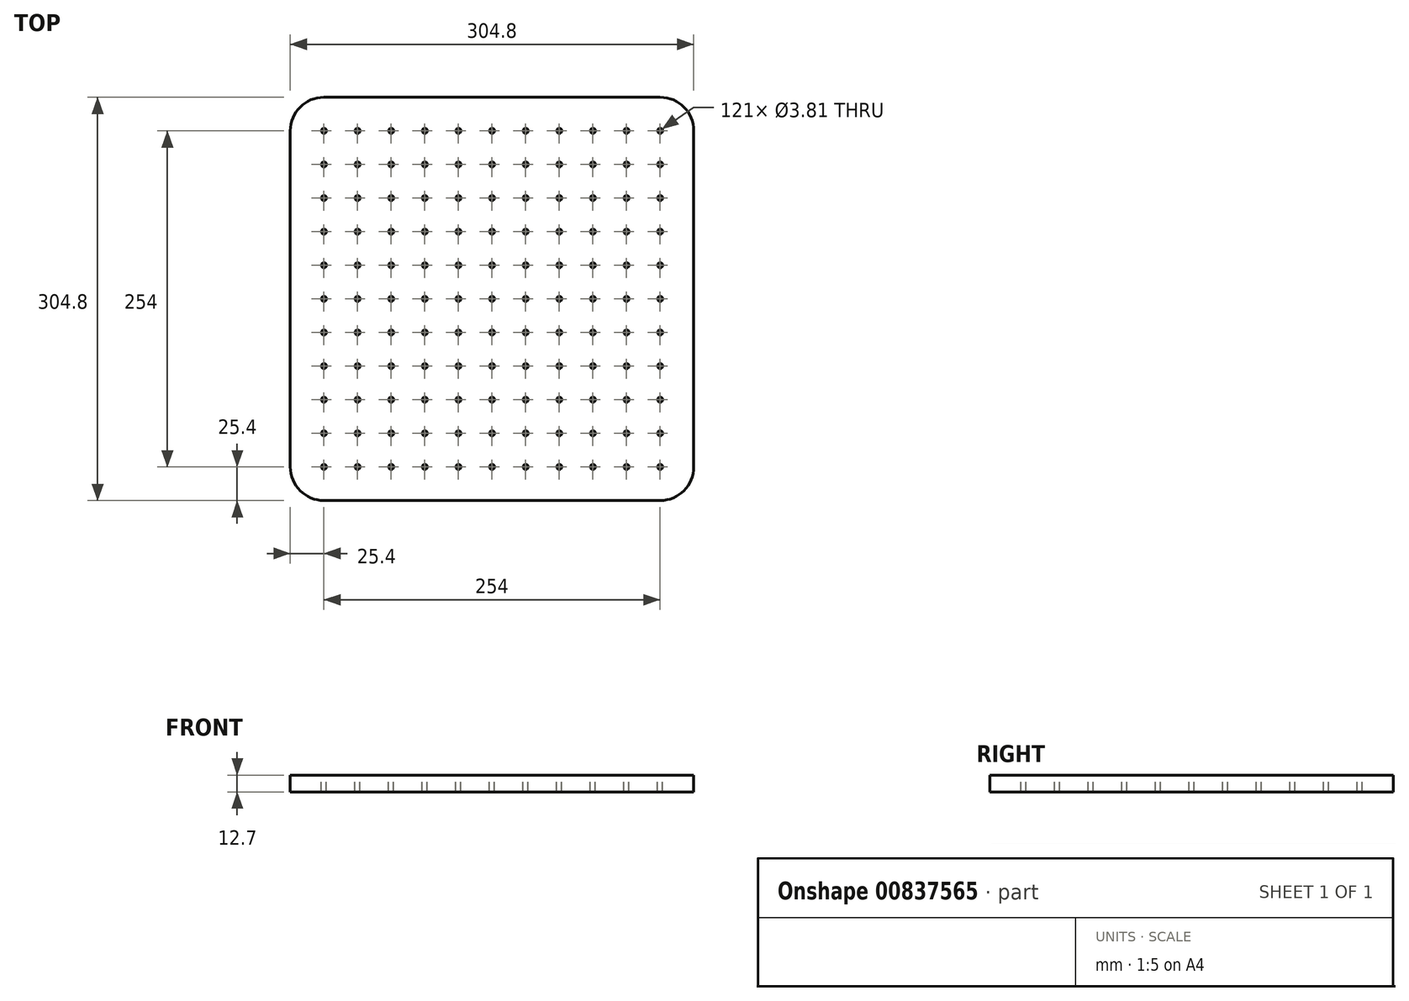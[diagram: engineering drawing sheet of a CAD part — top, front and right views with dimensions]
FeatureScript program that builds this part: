
annotation { "Feature Type Name" : "Feature", "Feature Type Description" : "" }
export const myFeature = defineFeature(function(context is Context, id is Id, definition is map)
    precondition{}
    {
        {
            var Q0;
            Q0=qCreatedBy(makeId("Top.planeOp"),FACE);
            var sketch = newSketch(context, id + "F0", { "sketchPlane" : qUnion([Q0])});
            skLineSegment(sketch, "E0.bottom", {"start": v(127, 152.4) * mm, "end": v(-127, 152.4) * mm});
            skLineSegment(sketch, "E0.top", {"start": v(127, -152.4) * mm, "end": v(-127, -152.4) * mm});
            skLineSegment(sketch, "E0.left", {"start": v(152.4, 127) * mm, "end": v(152.4, -127) * mm});
            skLineSegment(sketch, "E0.right", {"start": v(-152.4, 127) * mm, "end": v(-152.4, -127) * mm});
            skPoint(sketch, "E0.middle", {"position": v(0, 0) * mm});
            skCircle(sketch, "E1", {"center": v(-127, 127) * mm, "radius": 1.9 * mm});
            skLineSegment(sketch, "E2", {"start": v(-127, 127) * mm, "end": v(-127, 152.4) * mm, "construction": true});
            skLineSegment(sketch, "E3", {"start": v(-152.4, 127) * mm, "end": v(-127, 127) * mm, "construction": true});
            skCircle(sketch, "E4.0.1.0", {"center": v(-127, 101.6) * mm, "radius": 1.9 * mm});
            skCircle(sketch, "E4.1.0.0", {"center": v(-101.6, 127) * mm, "radius": 1.9 * mm});
            skCircle(sketch, "E4.1.1.0", {"center": v(-101.6, 101.6) * mm, "radius": 1.9 * mm});
            skCircle(sketch, "E4.2.0.0", {"center": v(-76.2, 127) * mm, "radius": 1.9 * mm});
            skCircle(sketch, "E4.2.1.0", {"center": v(-76.2, 101.6) * mm, "radius": 1.9 * mm});
            skLineSegment(sketch, "E4.direction1", {"start": v(-127, 127) * mm, "end": v(-101.6, 127) * mm, "construction": true});
            skLineSegment(sketch, "E4.direction2", {"start": v(-127, 127) * mm, "end": v(-127, 101.6) * mm, "construction": true});
            skCircle(sketch, "E5.0.0.2", {"center": v(-127, 76.2) * mm, "radius": 1.9 * mm});
            skCircle(sketch, "E5.0.0.3", {"center": v(-127, 50.8) * mm, "radius": 1.9 * mm});
            skCircle(sketch, "E5.0.0.4", {"center": v(-127, 25.4) * mm, "radius": 1.9 * mm});
            skCircle(sketch, "E5.0.0.5", {"center": v(-127, 0) * mm, "radius": 1.9 * mm});
            skCircle(sketch, "E5.0.0.6", {"center": v(-127, -25.4) * mm, "radius": 1.9 * mm});
            skCircle(sketch, "E5.0.0.7", {"center": v(-127, -50.8) * mm, "radius": 1.9 * mm});
            skCircle(sketch, "E5.0.0.8", {"center": v(-127, -76.2) * mm, "radius": 1.9 * mm});
            skCircle(sketch, "E5.0.0.9", {"center": v(-127, -101.6) * mm, "radius": 1.9 * mm});
            skCircle(sketch, "E5.0.1.2", {"center": v(-101.6, 76.2) * mm, "radius": 1.9 * mm});
            skCircle(sketch, "E5.0.1.3", {"center": v(-101.6, 50.8) * mm, "radius": 1.9 * mm});
            skCircle(sketch, "E5.0.1.4", {"center": v(-101.6, 25.4) * mm, "radius": 1.9 * mm});
            skCircle(sketch, "E5.0.1.5", {"center": v(-101.6, 0) * mm, "radius": 1.9 * mm});
            skCircle(sketch, "E5.0.1.6", {"center": v(-101.6, -25.4) * mm, "radius": 1.9 * mm});
            skCircle(sketch, "E5.0.1.7", {"center": v(-101.6, -50.8) * mm, "radius": 1.9 * mm});
            skCircle(sketch, "E5.0.1.8", {"center": v(-101.6, -76.2) * mm, "radius": 1.9 * mm});
            skCircle(sketch, "E5.0.1.9", {"center": v(-101.6, -101.6) * mm, "radius": 1.9 * mm});
            skCircle(sketch, "E5.0.2.2", {"center": v(-76.2, 76.2) * mm, "radius": 1.9 * mm});
            skCircle(sketch, "E5.0.2.3", {"center": v(-76.2, 50.8) * mm, "radius": 1.9 * mm});
            skCircle(sketch, "E5.0.2.4", {"center": v(-76.2, 25.4) * mm, "radius": 1.9 * mm});
            skCircle(sketch, "E5.0.2.5", {"center": v(-76.2, 0) * mm, "radius": 1.9 * mm});
            skCircle(sketch, "E5.0.2.6", {"center": v(-76.2, -25.4) * mm, "radius": 1.9 * mm});
            skCircle(sketch, "E5.0.2.7", {"center": v(-76.2, -50.8) * mm, "radius": 1.9 * mm});
            skCircle(sketch, "E5.0.2.8", {"center": v(-76.2, -76.2) * mm, "radius": 1.9 * mm});
            skCircle(sketch, "E5.0.2.9", {"center": v(-76.2, -101.6) * mm, "radius": 1.9 * mm});
            skCircle(sketch, "E6.0.0.10", {"center": v(-127, -127) * mm, "radius": 1.9 * mm});
            skCircle(sketch, "E6.0.1.10", {"center": v(-101.6, -127) * mm, "radius": 1.9 * mm});
            skCircle(sketch, "E6.0.2.10", {"center": v(-76.2, -127) * mm, "radius": 1.9 * mm});
            skCircle(sketch, "E7.0.3.0", {"center": v(-50.8, 127) * mm, "radius": 1.9 * mm});
            skCircle(sketch, "E7.0.3.1", {"center": v(-50.8, 101.6) * mm, "radius": 1.9 * mm});
            skCircle(sketch, "E7.0.3.2", {"center": v(-50.8, 76.2) * mm, "radius": 1.9 * mm});
            skCircle(sketch, "E7.0.3.3", {"center": v(-50.8, 50.8) * mm, "radius": 1.9 * mm});
            skCircle(sketch, "E7.0.3.4", {"center": v(-50.8, 25.4) * mm, "radius": 1.9 * mm});
            skCircle(sketch, "E7.0.3.5", {"center": v(-50.8, 0) * mm, "radius": 1.9 * mm});
            skCircle(sketch, "E7.0.3.6", {"center": v(-50.8, -25.4) * mm, "radius": 1.9 * mm});
            skCircle(sketch, "E7.0.3.7", {"center": v(-50.8, -50.8) * mm, "radius": 1.9 * mm});
            skCircle(sketch, "E7.0.3.8", {"center": v(-50.8, -76.2) * mm, "radius": 1.9 * mm});
            skCircle(sketch, "E7.0.3.9", {"center": v(-50.8, -101.6) * mm, "radius": 1.9 * mm});
            skCircle(sketch, "E7.0.3.10", {"center": v(-50.8, -127) * mm, "radius": 1.9 * mm});
            skCircle(sketch, "E7.0.4.0", {"center": v(-25.4, 127) * mm, "radius": 1.9 * mm});
            skCircle(sketch, "E7.0.4.1", {"center": v(-25.4, 101.6) * mm, "radius": 1.9 * mm});
            skCircle(sketch, "E7.0.4.2", {"center": v(-25.4, 76.2) * mm, "radius": 1.9 * mm});
            skCircle(sketch, "E7.0.4.3", {"center": v(-25.4, 50.8) * mm, "radius": 1.9 * mm});
            skCircle(sketch, "E7.0.4.4", {"center": v(-25.4, 25.4) * mm, "radius": 1.9 * mm});
            skCircle(sketch, "E7.0.4.5", {"center": v(-25.4, 0) * mm, "radius": 1.9 * mm});
            skCircle(sketch, "E7.0.4.6", {"center": v(-25.4, -25.4) * mm, "radius": 1.9 * mm});
            skCircle(sketch, "E7.0.4.7", {"center": v(-25.4, -50.8) * mm, "radius": 1.9 * mm});
            skCircle(sketch, "E7.0.4.8", {"center": v(-25.4, -76.2) * mm, "radius": 1.9 * mm});
            skCircle(sketch, "E7.0.4.9", {"center": v(-25.4, -101.6) * mm, "radius": 1.9 * mm});
            skCircle(sketch, "E7.0.4.10", {"center": v(-25.4, -127) * mm, "radius": 1.9 * mm});
            skCircle(sketch, "E7.0.5.0", {"center": v(0, 127) * mm, "radius": 1.9 * mm});
            skCircle(sketch, "E7.0.5.1", {"center": v(0, 101.6) * mm, "radius": 1.9 * mm});
            skCircle(sketch, "E7.0.5.2", {"center": v(0, 76.2) * mm, "radius": 1.9 * mm});
            skCircle(sketch, "E7.0.5.3", {"center": v(0, 50.8) * mm, "radius": 1.9 * mm});
            skCircle(sketch, "E7.0.5.4", {"center": v(0, 25.4) * mm, "radius": 1.9 * mm});
            skCircle(sketch, "E7.0.5.5", {"center": v(0, 0) * mm, "radius": 1.9 * mm});
            skCircle(sketch, "E7.0.5.6", {"center": v(0, -25.4) * mm, "radius": 1.9 * mm});
            skCircle(sketch, "E7.0.5.7", {"center": v(0, -50.8) * mm, "radius": 1.9 * mm});
            skCircle(sketch, "E7.0.5.8", {"center": v(0, -76.2) * mm, "radius": 1.9 * mm});
            skCircle(sketch, "E7.0.5.9", {"center": v(0, -101.6) * mm, "radius": 1.9 * mm});
            skCircle(sketch, "E7.0.5.10", {"center": v(0, -127) * mm, "radius": 1.9 * mm});
            skCircle(sketch, "E7.0.6.0", {"center": v(25.4, 127) * mm, "radius": 1.9 * mm});
            skCircle(sketch, "E7.0.6.1", {"center": v(25.4, 101.6) * mm, "radius": 1.9 * mm});
            skCircle(sketch, "E7.0.6.2", {"center": v(25.4, 76.2) * mm, "radius": 1.9 * mm});
            skCircle(sketch, "E7.0.6.3", {"center": v(25.4, 50.8) * mm, "radius": 1.9 * mm});
            skCircle(sketch, "E7.0.6.4", {"center": v(25.4, 25.4) * mm, "radius": 1.9 * mm});
            skCircle(sketch, "E7.0.6.5", {"center": v(25.4, 0) * mm, "radius": 1.9 * mm});
            skCircle(sketch, "E7.0.6.6", {"center": v(25.4, -25.4) * mm, "radius": 1.9 * mm});
            skCircle(sketch, "E7.0.6.7", {"center": v(25.4, -50.8) * mm, "radius": 1.9 * mm});
            skCircle(sketch, "E7.0.6.8", {"center": v(25.4, -76.2) * mm, "radius": 1.9 * mm});
            skCircle(sketch, "E7.0.6.9", {"center": v(25.4, -101.6) * mm, "radius": 1.9 * mm});
            skCircle(sketch, "E7.0.6.10", {"center": v(25.4, -127) * mm, "radius": 1.9 * mm});
            skCircle(sketch, "E7.0.7.0", {"center": v(50.8, 127) * mm, "radius": 1.9 * mm});
            skCircle(sketch, "E7.0.7.1", {"center": v(50.8, 101.6) * mm, "radius": 1.9 * mm});
            skCircle(sketch, "E7.0.7.2", {"center": v(50.8, 76.2) * mm, "radius": 1.9 * mm});
            skCircle(sketch, "E7.0.7.3", {"center": v(50.8, 50.8) * mm, "radius": 1.9 * mm});
            skCircle(sketch, "E7.0.7.4", {"center": v(50.8, 25.4) * mm, "radius": 1.9 * mm});
            skCircle(sketch, "E7.0.7.5", {"center": v(50.8, 0) * mm, "radius": 1.9 * mm});
            skCircle(sketch, "E7.0.7.6", {"center": v(50.8, -25.4) * mm, "radius": 1.9 * mm});
            skCircle(sketch, "E7.0.7.7", {"center": v(50.8, -50.8) * mm, "radius": 1.9 * mm});
            skCircle(sketch, "E7.0.7.8", {"center": v(50.8, -76.2) * mm, "radius": 1.9 * mm});
            skCircle(sketch, "E7.0.7.9", {"center": v(50.8, -101.6) * mm, "radius": 1.9 * mm});
            skCircle(sketch, "E7.0.7.10", {"center": v(50.8, -127) * mm, "radius": 1.9 * mm});
            skCircle(sketch, "E7.0.8.0", {"center": v(76.2, 127) * mm, "radius": 1.9 * mm});
            skCircle(sketch, "E7.0.8.1", {"center": v(76.2, 101.6) * mm, "radius": 1.9 * mm});
            skCircle(sketch, "E7.0.8.2", {"center": v(76.2, 76.2) * mm, "radius": 1.9 * mm});
            skCircle(sketch, "E7.0.8.3", {"center": v(76.2, 50.8) * mm, "radius": 1.9 * mm});
            skCircle(sketch, "E7.0.8.4", {"center": v(76.2, 25.4) * mm, "radius": 1.9 * mm});
            skCircle(sketch, "E7.0.8.5", {"center": v(76.2, 0) * mm, "radius": 1.9 * mm});
            skCircle(sketch, "E7.0.8.6", {"center": v(76.2, -25.4) * mm, "radius": 1.9 * mm});
            skCircle(sketch, "E7.0.8.7", {"center": v(76.2, -50.8) * mm, "radius": 1.9 * mm});
            skCircle(sketch, "E7.0.8.8", {"center": v(76.2, -76.2) * mm, "radius": 1.9 * mm});
            skCircle(sketch, "E7.0.8.9", {"center": v(76.2, -101.6) * mm, "radius": 1.9 * mm});
            skCircle(sketch, "E7.0.8.10", {"center": v(76.2, -127) * mm, "radius": 1.9 * mm});
            skCircle(sketch, "E7.0.9.0", {"center": v(101.6, 127) * mm, "radius": 1.9 * mm});
            skCircle(sketch, "E7.0.9.1", {"center": v(101.6, 101.6) * mm, "radius": 1.9 * mm});
            skCircle(sketch, "E7.0.9.2", {"center": v(101.6, 76.2) * mm, "radius": 1.9 * mm});
            skCircle(sketch, "E7.0.9.3", {"center": v(101.6, 50.8) * mm, "radius": 1.9 * mm});
            skCircle(sketch, "E7.0.9.4", {"center": v(101.6, 25.4) * mm, "radius": 1.9 * mm});
            skCircle(sketch, "E7.0.9.5", {"center": v(101.6, 0) * mm, "radius": 1.9 * mm});
            skCircle(sketch, "E7.0.9.6", {"center": v(101.6, -25.4) * mm, "radius": 1.9 * mm});
            skCircle(sketch, "E7.0.9.7", {"center": v(101.6, -50.8) * mm, "radius": 1.9 * mm});
            skCircle(sketch, "E7.0.9.8", {"center": v(101.6, -76.2) * mm, "radius": 1.9 * mm});
            skCircle(sketch, "E7.0.9.9", {"center": v(101.6, -101.6) * mm, "radius": 1.9 * mm});
            skCircle(sketch, "E7.0.9.10", {"center": v(101.6, -127) * mm, "radius": 1.9 * mm});
            skCircle(sketch, "E7.0.10.0", {"center": v(127, 127) * mm, "radius": 1.9 * mm});
            skCircle(sketch, "E7.0.10.1", {"center": v(127, 101.6) * mm, "radius": 1.9 * mm});
            skCircle(sketch, "E7.0.10.2", {"center": v(127, 76.2) * mm, "radius": 1.9 * mm});
            skCircle(sketch, "E7.0.10.3", {"center": v(127, 50.8) * mm, "radius": 1.9 * mm});
            skCircle(sketch, "E7.0.10.4", {"center": v(127, 25.4) * mm, "radius": 1.9 * mm});
            skCircle(sketch, "E7.0.10.5", {"center": v(127, 0) * mm, "radius": 1.9 * mm});
            skCircle(sketch, "E7.0.10.6", {"center": v(127, -25.4) * mm, "radius": 1.9 * mm});
            skCircle(sketch, "E7.0.10.7", {"center": v(127, -50.8) * mm, "radius": 1.9 * mm});
            skCircle(sketch, "E7.0.10.8", {"center": v(127, -76.2) * mm, "radius": 1.9 * mm});
            skCircle(sketch, "E7.0.10.9", {"center": v(127, -101.6) * mm, "radius": 1.9 * mm});
            skCircle(sketch, "E7.0.10.10", {"center": v(127, -127) * mm, "radius": 1.9 * mm});
            skPoint(sketch, "E8.visualSharp", {"position": v(-152.4, 152.4) * mm});
            skArc(sketch, "E8.filletArc", {"start": v(-127, 152.4) * mm, "mid": v(-144.96, 144.96) * mm, "end": v(-152.4, 127) * mm});
            skPoint(sketch, "E9.visualSharp", {"position": v(152.4, 152.4) * mm});
            skArc(sketch, "E9.filletArc", {"start": v(152.4, 127) * mm, "mid": v(144.96, 144.96) * mm, "end": v(127, 152.4) * mm});
            skPoint(sketch, "E10.visualSharp", {"position": v(152.4, -152.4) * mm});
            skArc(sketch, "E10.filletArc", {"start": v(127, -152.4) * mm, "mid": v(144.96, -144.96) * mm, "end": v(152.4, -127) * mm});
            skPoint(sketch, "E11.visualSharp", {"position": v(-152.4, -152.4) * mm});
            skArc(sketch, "E11.filletArc", {"start": v(-152.4, -127) * mm, "mid": v(-144.96, -144.96) * mm, "end": v(-127, -152.4) * mm});
            skSolve(sketch);
        }
        {
            var Q0;
            Q0=makeQuery(id+"F0.imprint","IMPRINT",FACE,{"disambiguationData":[TD([[makeQuery(id+"F0.imprint","IMPRINT",EDGE,{"derivedFrom":sQuery(id+"F0.wireOp",EDGE,"E0.bottom")}),1.0]])]});
            extrude(context, id + "F1", {"entities" : qUnion([Q0]), "oppositeDirection" : true, "depth" : 12.7 * mm, "offsetDistance" : 25.4 * mm});
        }
    });
